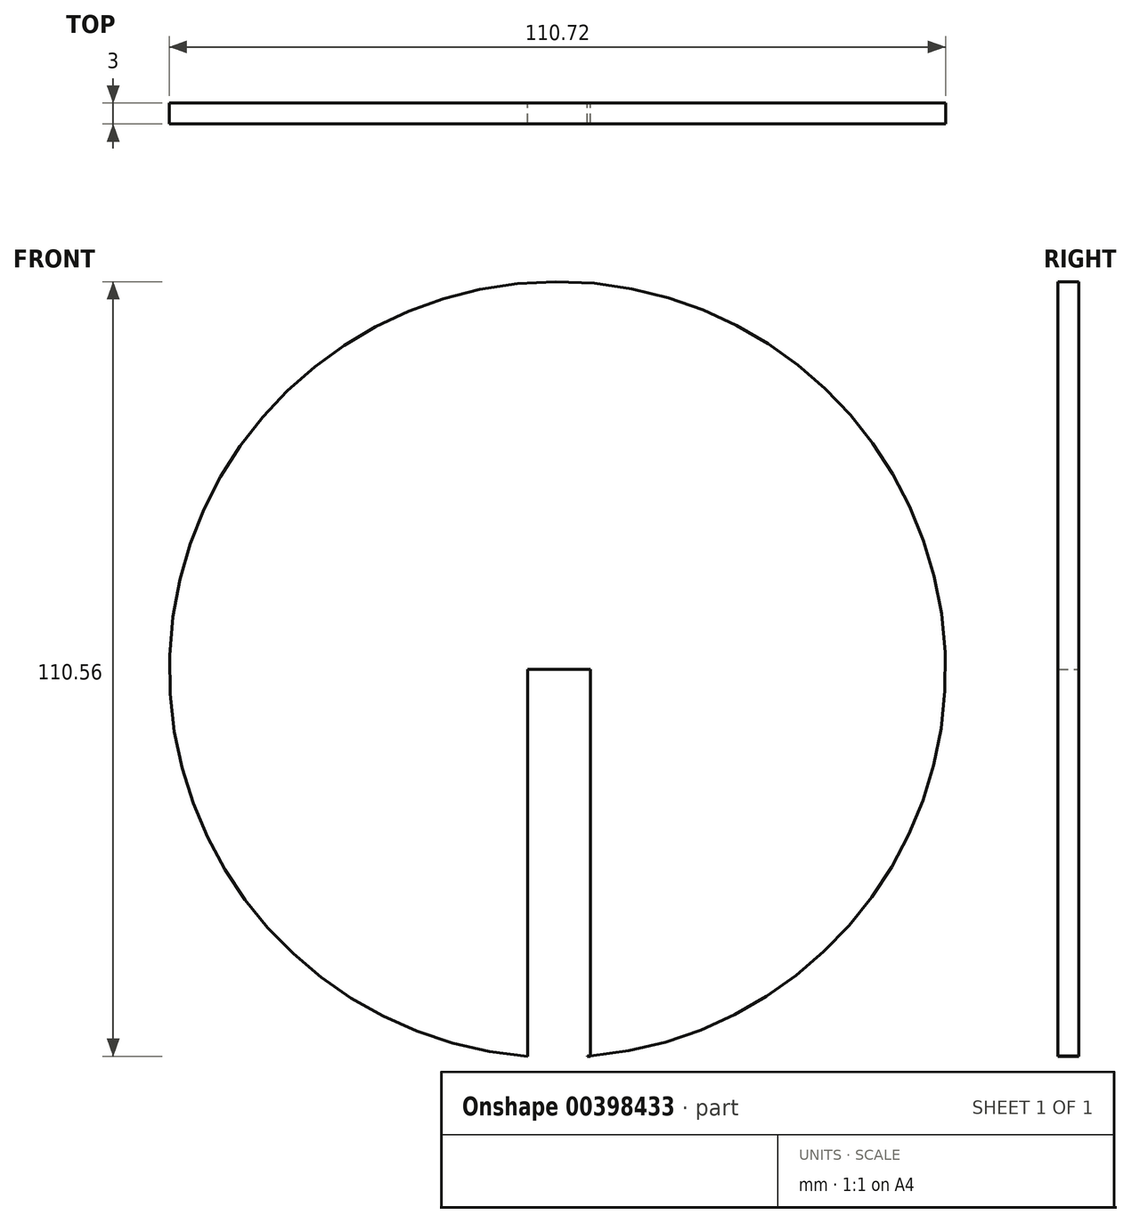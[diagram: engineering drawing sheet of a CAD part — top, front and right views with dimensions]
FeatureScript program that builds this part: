
annotation { "Feature Type Name" : "Feature", "Feature Type Description" : "" }
export const myFeature = defineFeature(function(context is Context, id is Id, definition is map)
    precondition{}
    {
        {
            var Q0;
            Q0=qCreatedBy(makeId("Front.planeOp"),FACE);
            var sketch = newSketch(context, id + "F0", { "sketchPlane" : qUnion([Q0])});
            skArc(sketch, "E0", {"start": v(4.25, -55.2) * mm, "mid": v(0, 55.36) * mm, "end": v(-4.25, -55.2) * mm});
            skLineSegment(sketch, "E1.bottom", {"start": v(4.25, -55.2) * mm, "end": v(4.7, -55.2) * mm});
            skLineSegment(sketch, "E1.top", {"start": v(-4.25, 0) * mm, "end": v(4.7, 0) * mm});
            skLineSegment(sketch, "E1.left", {"start": v(-4.25, -55.2) * mm, "end": v(-4.25, 0) * mm});
            skLineSegment(sketch, "E1.right", {"start": v(4.7, -55.2) * mm, "end": v(4.7, 0) * mm});
            skSolve(sketch);
        }
        {
            var Q0;
            Q0 = qSketchRegion(id + "F0", true);
            extrude(context, id + "F1", {"entities" : qUnion([Q0]), "depth" : 3 * mm});
        }
    });
